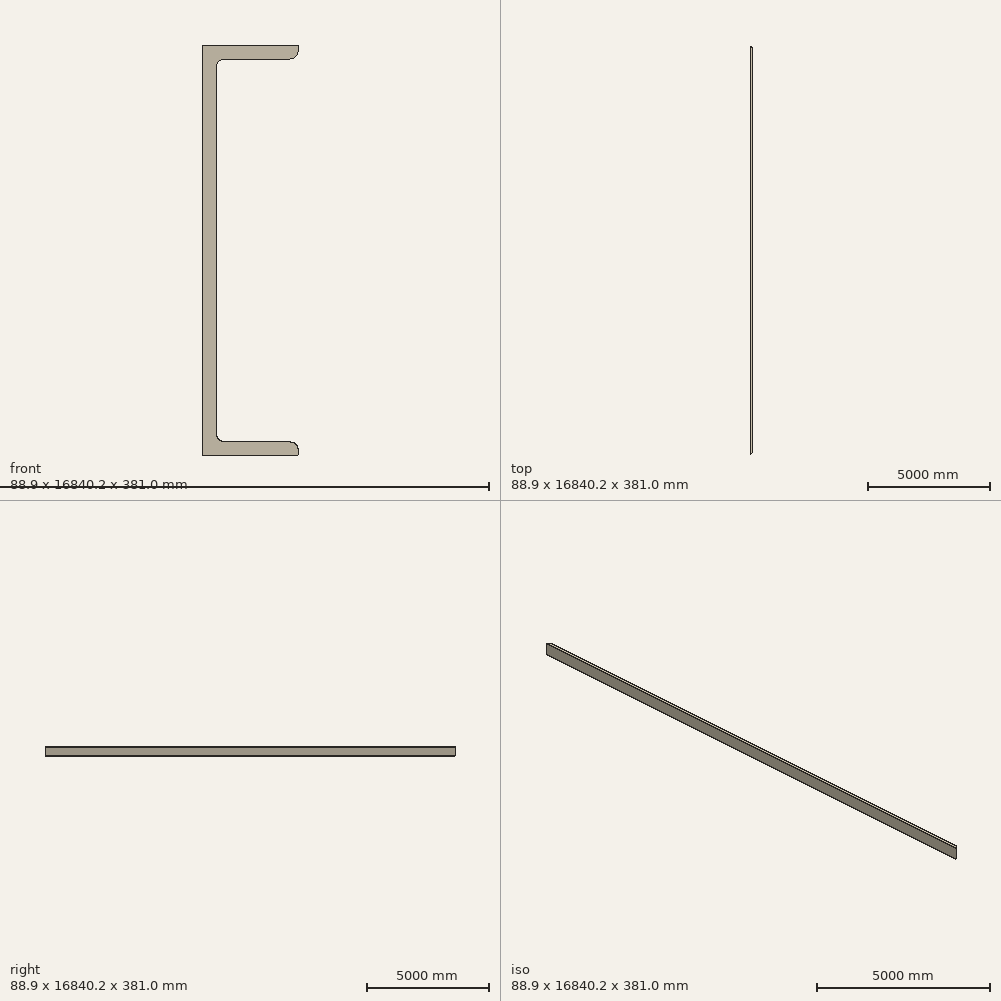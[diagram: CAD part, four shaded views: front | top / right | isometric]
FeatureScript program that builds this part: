
annotation { "Feature Type Name" : "Feature", "Feature Type Description" : "" }
export const myFeature = defineFeature(function(context is Context, id is Id, definition is map)
    precondition{}
    {
        {
            var Q0;
            Q0=qCreatedBy(makeId("Front.planeOp"),FACE);
            var sketch = newSketch(context, id + "F0", { "sketchPlane" : qUnion([Q0])});
            skLineSegment(sketch, "E0", {"start": v(44.45, 190.5) * mm, "end": v(-44.45, 190.5) * mm});
            skLineSegment(sketch, "E1", {"start": v(-44.45, 190.5) * mm, "end": v(-44.45, -190.5) * mm});
            skLineSegment(sketch, "E2", {"start": v(-44.45, -190.5) * mm, "end": v(44.45, -190.5) * mm});
            skLineSegment(sketch, "E3", {"start": v(44.45, -190.5) * mm, "end": v(44.45, -177.8) * mm});
            skLineSegment(sketch, "E4", {"start": v(44.45, -177.8) * mm, "end": v(-31.75, -177.8) * mm});
            skLineSegment(sketch, "E5", {"start": v(-31.75, -177.8) * mm, "end": v(-31.75, 177.8) * mm});
            skLineSegment(sketch, "E6", {"start": v(-31.75, 177.8) * mm, "end": v(44.45, 177.8) * mm});
            skLineSegment(sketch, "E7", {"start": v(44.45, 177.8) * mm, "end": v(44.45, 190.5) * mm});
            skSolve(sketch);
        }
        {
            var Q0;
            Q0=makeQuery(id+"F0.imprint","IMPRINT",FACE,{"disambiguationData":[TD([[makeQuery(id+"F0.imprint","IMPRINT",EDGE,{"derivedFrom":sQuery(id+"F0.wireOp",EDGE,"E0")}),1.0]])]});
            extrude(context, id + "F1", {"entities" : qUnion([Q0]), "depth" : 16764 * mm + 76.2 * mm, "offsetDistance" : 25.4 * mm});
        }
        {
            var Q0;
            Q0=makeQuery(id+"F1.opExtrude","SWEPT_EDGE",EDGE,{"disambiguationData":[OSD([sQuery(id+"F0.wireOp",EDGE,"E3"),sQuery(id+"F0.wireOp",EDGE,"E4")])]});
            var Q1;
            Q1=makeQuery(id+"F1.opExtrude","SWEPT_EDGE",EDGE,{"disambiguationData":[OSD([sQuery(id+"F0.wireOp",EDGE,"E4"),sQuery(id+"F0.wireOp",EDGE,"E5")])]});
            var Q2;
            Q2=makeQuery(id+"F1.opExtrude","SWEPT_EDGE",EDGE,{"disambiguationData":[OSD([sQuery(id+"F0.wireOp",EDGE,"E5"),sQuery(id+"F0.wireOp",EDGE,"E6")])]});
            var Q3;
            Q3=makeQuery(id+"F1.opExtrude","SWEPT_EDGE",EDGE,{"disambiguationData":[OSD([sQuery(id+"F0.wireOp",EDGE,"E6"),sQuery(id+"F0.wireOp",EDGE,"E7")])]});
            fillet(context, id + "F2", {"entities" : qUnion([Q0, Q1, Q2, Q3]), "radius" : 7.62 * mm, "tangentPropagation" : true, "allowEdgeOverflow" : false});
        }
        {
            var Q0;
            Q0=makeQuery(id+"F1.opExtrude","SWEPT_FACE",FACE,{"disambiguationData":[OSD([sQuery(id+"F0.wireOp",EDGE,"E0")])]});
            var sketch = newSketch(context, id + "F3", { "sketchPlane" : qUnion([Q0])});
            skLineSegment(sketch, "E8", {"start": v(-44.45, 0) * mm, "end": v(44.45, -88.9) * mm});
            skLineSegment(sketch, "E9", {"start": v(-44.45, -16840.2) * mm, "end": v(44.45, -16751.3) * mm});
            skSolve(sketch);
        }
        {
            var Q0;
            {var subQ0=sQuery(id+"F3.wireOp",EDGE,"E8");Q0=makeQuery(id+"F3.imprint","IMPRINT",FACE,{"disambiguationData":[TD([[makeQuery(id+"F3.imprint","IMPRINT",EDGE,{"derivedFrom":subQ0}),1.0]])]});}
            extrude(context, id + "F4", {"entities" : qUnion([Q0]), "operationType" : NewBodyOperationType.REMOVE, "endBound" : BoundingType.THROUGH_ALL, "oppositeDirection" : true, "depth" : 25.4 * mm, "offsetDistance" : 25.4 * mm});
        }
        {
            var Q0;
            {var subQ0=sQuery(id+"F3.wireOp",EDGE,"E9");Q0=makeQuery(id+"F3.imprint","IMPRINT",FACE,{"disambiguationData":[TD([[makeQuery(id+"F3.imprint","IMPRINT",EDGE,{"derivedFrom":subQ0}),-1.0]])]});}
            extrude(context, id + "F5", {"entities" : qUnion([Q0]), "operationType" : NewBodyOperationType.REMOVE, "endBound" : BoundingType.THROUGH_ALL, "oppositeDirection" : true, "depth" : 25.4 * mm, "offsetDistance" : 25.4 * mm});
        }
    });
